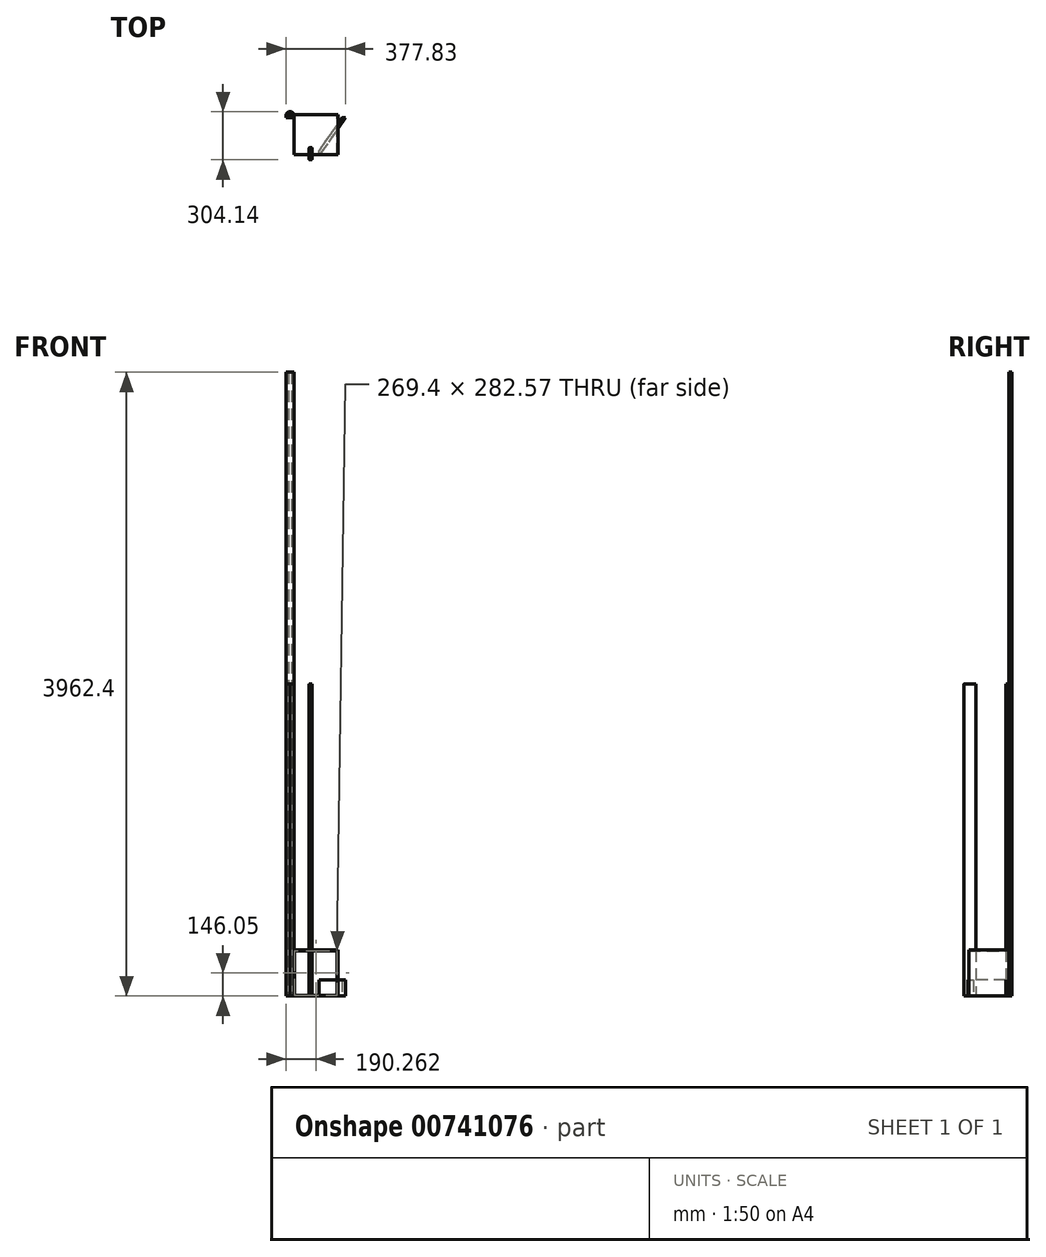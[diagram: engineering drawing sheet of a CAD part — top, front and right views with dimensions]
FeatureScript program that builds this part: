
annotation { "Feature Type Name" : "Feature", "Feature Type Description" : "" }
export const myFeature = defineFeature(function(context is Context, id is Id, definition is map)
    precondition{}
    {
        {
            var Q0;
            Q0=qCreatedBy(makeId("Front.planeOp"),FACE);
            var sketch = newSketch(context, id + "F0", { "sketchPlane" : qUnion([Q0])});
            skLineSegment(sketch, "E0.bottom", {"start": v(0, 0) * mm, "end": v(278.92, 0) * mm});
            skLineSegment(sketch, "E0.top", {"start": v(0, 292.1) * mm, "end": v(278.92, 292.1) * mm});
            skLineSegment(sketch, "E0.left", {"start": v(0, 0) * mm, "end": v(0, 292.1) * mm});
            skLineSegment(sketch, "E0.right", {"start": v(278.92, 0) * mm, "end": v(278.92, 292.1) * mm});
            skLineSegment(sketch, "E1.0", {"start": v(4.76, 287.34) * mm, "end": v(274.16, 287.34) * mm});
            skLineSegment(sketch, "E1.1", {"start": v(4.76, 4.76) * mm, "end": v(4.76, 287.34) * mm});
            skLineSegment(sketch, "E1.2", {"start": v(4.76, 4.76) * mm, "end": v(274.16, 4.76) * mm});
            skLineSegment(sketch, "E1.3", {"start": v(274.16, 4.76) * mm, "end": v(274.16, 287.34) * mm});
            skSolve(sketch);
        }
        {
            var Q0;
            Q0=makeQuery(id+"F0.imprint","IMPRINT",FACE,{"disambiguationData":[TD([[makeQuery(id+"F0.imprint","IMPRINT",EDGE,{"derivedFrom":sQuery(id+"F0.wireOp",EDGE,"E0.bottom")}),1.0]])]});
            extrude(context, id + "F1", {"entities" : qUnion([Q0]), "depth" : 254 * mm, "offsetDistance" : 25.4 * mm});
        }
        {
            var Q0;
            Q0=qCreatedBy(makeId("Top.planeOp"),FACE);
            var sketch = newSketch(context, id + "F2", { "sketchPlane" : qUnion([Q0])});
            skLineSegment(sketch, "E2.bottom", {"start": v(0, 0) * mm, "end": v(-50.8, 0) * mm});
            skLineSegment(sketch, "E2.top", {"start": v(0, 19.05) * mm, "end": v(-50.8, 19.05) * mm});
            skLineSegment(sketch, "E2.left", {"start": v(0, 0) * mm, "end": v(0, 19.05) * mm});
            skLineSegment(sketch, "E2.right", {"start": v(-50.8, 0) * mm, "end": v(-50.8, 19.05) * mm});
            skLineSegment(sketch, "E3", {"start": v(-50.8, 0) * mm, "end": v(-50.8, -19.05) * mm});
            skLineSegment(sketch, "E4", {"start": v(-50.8, -19.05) * mm, "end": v(0, -19.05) * mm});
            skLineSegment(sketch, "E5", {"start": v(0, -19.05) * mm, "end": v(0, 0) * mm});
            skLineSegment(sketch, "E6", {"start": v(0, 3.17) * mm, "end": v(-15.88, 19.05) * mm});
            skLineSegment(sketch, "E7", {"start": v(-50.8, 3.17) * mm, "end": v(-34.93, 19.05) * mm});
            skLineSegment(sketch, "E8", {"start": v(-25.4, -19.05) * mm, "end": v(-25.4, 0) * mm});
            skSolve(sketch);
        }
        {
            var Q0;
            {var subQ0=sQuery(id+"F2.wireOp",EDGE,"E6");Q0=makeQuery(id+"F2.imprint","IMPRINT",FACE,{"disambiguationData":[TD([[makeQuery(id+"F2.imprint","IMPRINT",EDGE,{"derivedFrom":subQ0}),1.0]])]});}
            var Q1;
            {var subQ0=sQuery(id+"F2.wireOp",EDGE,"E3");Q1=makeQuery(id+"F2.imprint","IMPRINT",FACE,{"disambiguationData":[TD([[makeQuery(id+"F2.imprint","IMPRINT",EDGE,{"derivedFrom":subQ0}),1.0]])]});}
            extrude(context, id + "F3", {"entities" : qUnion([Q0, Q1]), "depth" : 1981.2 * mm, "offsetDistance" : 25.4 * mm});
        }
        {
            var Q0;
            {var subQ0=sQuery(id+"F2.wireOp",EDGE,"E6");Q0=makeQuery(id+"F2.imprint","IMPRINT",FACE,{"disambiguationData":[TD([[makeQuery(id+"F2.imprint","IMPRINT",EDGE,{"derivedFrom":subQ0}),1.0]])]});}
            var Q1;
            {var subQ0=sQuery(id+"F2.wireOp",EDGE,"E5");Q1=makeQuery(id+"F2.imprint","IMPRINT",FACE,{"disambiguationData":[TD([[makeQuery(id+"F2.imprint","IMPRINT",EDGE,{"derivedFrom":subQ0}),1.0]])]});}
            extrude(context, id + "F4", {"entities" : qUnion([Q0, Q1]), "depth" : 1981.2 * mm, "offsetDistance" : 25.4 * mm});
        }
        {
            var Q0;
            Q0=qCreatedBy(makeId("Top.planeOp"),FACE);
            var sketch = newSketch(context, id + "F5", { "sketchPlane" : qUnion([Q0])});
            skLineSegment(sketch, "E9.bottom", {"start": v(99.36, -285.09) * mm, "end": v(112.06, -285.09) * mm});
            skLineSegment(sketch, "E9.top", {"start": v(99.36, -208.89) * mm, "end": v(112.06, -208.89) * mm});
            skLineSegment(sketch, "E9.left", {"start": v(96.19, -281.91) * mm, "end": v(96.19, -212.06) * mm});
            skLineSegment(sketch, "E9.right", {"start": v(115.24, -281.91) * mm, "end": v(115.24, -212.06) * mm});
            skPoint(sketch, "E10.visualSharp", {"position": v(115.24, -285.09) * mm});
            skArc(sketch, "E10.filletArc", {"start": v(112.06, -285.09) * mm, "mid": v(114.3, -284.16) * mm, "end": v(115.24, -281.91) * mm});
            skPoint(sketch, "E11.visualSharp", {"position": v(96.19, -285.09) * mm});
            skArc(sketch, "E11.filletArc", {"start": v(96.19, -281.91) * mm, "mid": v(97.12, -284.16) * mm, "end": v(99.36, -285.09) * mm});
            skPoint(sketch, "E12.visualSharp", {"position": v(115.24, -208.89) * mm});
            skArc(sketch, "E12.filletArc", {"start": v(115.24, -212.06) * mm, "mid": v(114.3, -209.82) * mm, "end": v(112.06, -208.89) * mm});
            skPoint(sketch, "E13.visualSharp", {"position": v(96.19, -208.89) * mm});
            skArc(sketch, "E13.filletArc", {"start": v(99.36, -208.89) * mm, "mid": v(97.12, -209.82) * mm, "end": v(96.19, -212.06) * mm});
            skSolve(sketch);
        }
        {
            var Q0;
            Q0 = qSketchRegion(id + "F5", true);
            extrude(context, id + "F6", {"entities" : qUnion([Q0]), "depth" : 1981.2 * mm, "offsetDistance" : 25.4 * mm});
        }
        {
            var Q0;
            Q0=qCreatedBy(makeId("Top.planeOp"),FACE);
            var sketch = newSketch(context, id + "F7", { "sketchPlane" : qUnion([Q0])});
            skLineSegment(sketch, "E14", {"start": v(0, 0) * mm, "end": v(330.2, 0) * mm});
            skLineSegment(sketch, "E15", {"start": v(330.2, 0) * mm, "end": v(330.2, -19.05) * mm});
            skLineSegment(sketch, "E16", {"start": v(327.03, -19.05) * mm, "end": v(330.2, -19.05) * mm});
            skLineSegment(sketch, "E17", {"start": v(327.03, -19.05) * mm, "end": v(139.7, -286.58) * mm});
            skLineSegment(sketch, "E18", {"start": v(139.7, -286.58) * mm, "end": v(139.7, 0) * mm});
            skLineSegment(sketch, "E19.0", {"start": v(311.42, -8.12) * mm, "end": v(124.1, -275.65) * mm});
            skLineSegment(sketch, "E20", {"start": v(327.03, -19.05) * mm, "end": v(303.77, -19.05) * mm});
            skLineSegment(sketch, "E21.0", {"start": v(158.75, -286.58) * mm, "end": v(158.75, 0) * mm});
            skSolve(sketch);
        }
        {
            var Q0;
            {var subQ0=sQuery(id+"F7.wireOp",EDGE,"E20");Q0=makeQuery(id+"F7.imprint","IMPRINT",FACE,{"disambiguationData":[TD([[makeQuery(id+"F7.imprint","IMPRINT",EDGE,{"derivedFrom":subQ0}),1.0]])]});}
            extrude(context, id + "F8", {"entities" : qUnion([Q0]), "depth" : 101.6 * mm, "offsetDistance" : 25.4 * mm});
        }
        {
            var Q0;
            Q0=makeQuery(id+"F3.opExtrude","CAP_FACE",FACE,{"disambiguationData":[OSD([sQuery(id+"F2.wireOp",EDGE,"E2.bottom"),sQuery(id+"F2.wireOp",EDGE,"E2.top"),sQuery(id+"F2.wireOp",EDGE,"E2.left"),sQuery(id+"F2.wireOp",EDGE,"E2.right"),sQuery(id+"F2.wireOp",EDGE,"E3"),sQuery(id+"F2.wireOp",EDGE,"E4"),sQuery(id+"F2.wireOp",EDGE,"E6"),sQuery(id+"F2.wireOp",EDGE,"E7"),sQuery(id+"F2.wireOp",EDGE,"E8")])],"isStart":false});
            var sketch = newSketch(context, id + "F9", { "sketchPlane" : qUnion([Q0])});
            skLineSegment(sketch, "E22.0.0", {"start": v(0, 3.17) * mm, "end": v(-15.88, 19.05) * mm});
            skLineSegment(sketch, "E22.0.1", {"start": v(-15.88, 19.05) * mm, "end": v(-34.93, 19.05) * mm});
            skLineSegment(sketch, "E22.0.2", {"start": v(-34.93, 19.05) * mm, "end": v(-50.8, 3.17) * mm});
            skLineSegment(sketch, "E22.0.3", {"start": v(-50.8, 3.17) * mm, "end": v(-50.8, -19.05) * mm});
            skLineSegment(sketch, "E22.0.4", {"start": v(-50.8, -19.05) * mm, "end": v(-25.4, -19.05) * mm});
            skLineSegment(sketch, "E22.0.5", {"start": v(-25.4, -19.05) * mm, "end": v(-25.4, 0) * mm});
            skLineSegment(sketch, "E22.0.6", {"start": v(-25.4, 0) * mm, "end": v(0, 0) * mm});
            skLineSegment(sketch, "E22.0.7", {"start": v(0, 0) * mm, "end": v(0, 3.17) * mm});
            skLineSegment(sketch, "E23", {"start": v(-25.4, 0) * mm, "end": v(-50.8, 0) * mm});
            skSolve(sketch);
        }
        {
            var Q0;
            Q0=makeQuery(id+"F9.imprint","IMPRINT",FACE,{"disambiguationData":[TD([[makeQuery(id+"F9.imprint","IMPRINT",EDGE,{"derivedFrom":sQuery(id+"F9.wireOp",EDGE,"E22.0.0")}),1.0]])]});
            extrude(context, id + "F10", {"entities" : qUnion([Q0]), "depth" : 1981.2 * mm, "offsetDistance" : 25.4 * mm});
        }
    });
